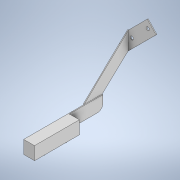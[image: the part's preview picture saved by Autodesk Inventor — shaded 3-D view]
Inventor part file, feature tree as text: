
AUTODESK INVENTOR PART (.ipt)
format: ipt  version: 2020 (Build 240168000, 168)  size: 179,712 bytes
history: native  units: mm
features: extrude x8, sketch x8, other x1
ambient origin geometry x8: Origin, YZ Plane, XZ Plane, XY Plane, X Axis, Y Axis, Z Axis, Center Point
bodies: Body1 (feature_tree), Body2 (feature_tree)
feature tree (17):
  other  "Sólido1"
  extrude  "Extrusión1"  Depth=81.8mm
  extrude  "Extrusión2"  Depth=143.0mm
  extrude  "Extrusión3"  Depth=1.55mm TaperAngle=0.0deg
  extrude  "Extrusión5"  Depth=32.8mm
  extrude  "Extrusión6"  Depth=23.3mm
  extrude  "Extrusión7"  Depth=1.55mm TaperAngle=0.0deg
  extrude  "Extrusión9"  Depth=1.55mm
  extrude  "Extrusión10"  Depth=23.3mm
  sketch  "Boceto1"  dims[d0=23.8mm d1=81.8mm]
  sketch  "Boceto2"  dims[d2=12.5mm d3=0.0mm d4=143.0mm]
  sketch  "Boceto3"  dims[d5=10.0mm d6=1.55mm d7=0.0mm]
  sketch  "Boceto6"  dims[d9=134.6mm d10=32.8mm]
  sketch  "Boceto7"  dims[d11=188.0mm d15=23.3mm]
  sketch  "Boceto8"  dims[d17=32.8mm d18=1.55mm d19=0.0mm]
  sketch  "Boceto11"  dims[d27=1.55mm d28=0.0mm d29=70.0mm]
  sketch  "Boceto13"  dims[d30=45.0deg d31=23.3mm d32=1.55mm d33=0.0mm d36=6.0mm d38=6.0mm d39=1.55mm d40=0.0mm d46=5.8mm d47=0.0mm d49=12.0mm d50=12.0mm d51=3.5mm d52=0.0mm]
